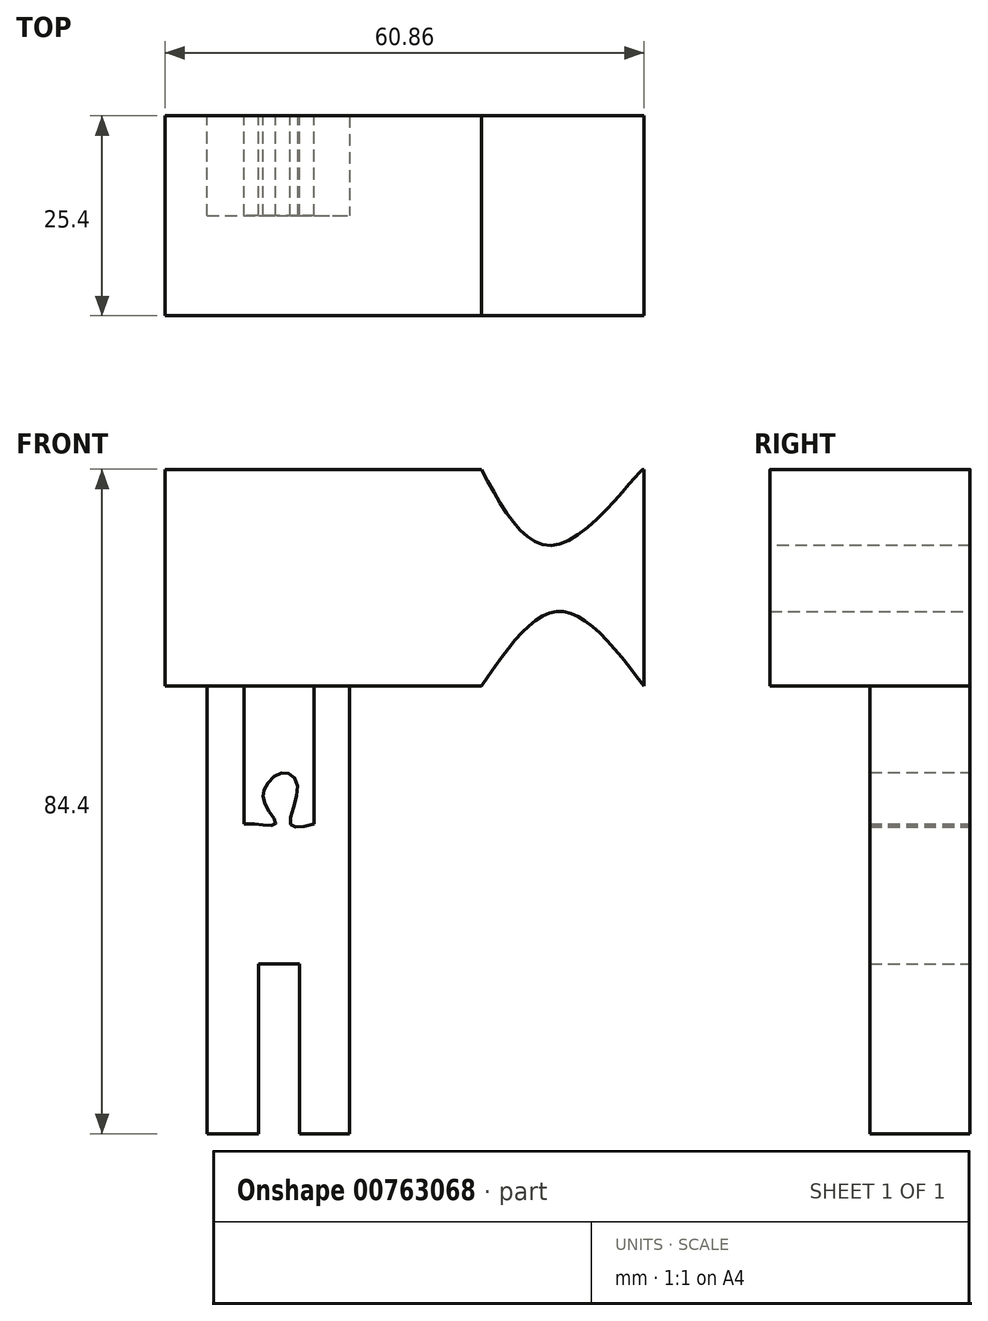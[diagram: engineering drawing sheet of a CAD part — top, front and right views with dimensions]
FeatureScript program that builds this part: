
annotation { "Feature Type Name" : "Feature", "Feature Type Description" : "" }
export const myFeature = defineFeature(function(context is Context, id is Id, definition is map)
    precondition{}
    {
        {
            var Q0;
            Q0=qCreatedBy(makeId("Front.planeOp"),FACE);
            var sketch = newSketch(context, id + "F0", { "sketchPlane" : qUnion([Q0])});
            skLineSegment(sketch, "E0", {"start": v(-46.17, 45.03) * mm, "end": v(-46.17, 17.54) * mm});
            skLineSegment(sketch, "E1", {"start": v(-46.17, 17.54) * mm, "end": v(-5.97, 17.54) * mm});
            skLineSegment(sketch, "E2", {"start": v(-46.17, 45.03) * mm, "end": v(-5.97, 45.03) * mm});
            skFitSpline(sketch, "E3", {"points": [v(-5.97, 45.03) * mm, v(3.89, 35.55) * mm, v(14.5, 45.03) * mm, v(14.7, 45.03) * mm], "startDerivative": vector(18.4, -33.95) * mm, "endDerivative": vector(2.33, -1.75) * mm});
            skFitSpline(sketch, "E4", {"points": [v(-5.97, 17.54) * mm, v(3.89, 27.02) * mm, v(14.7, 17.54) * mm], "startDerivative": vector(19.63, 28.56) * mm, "endDerivative": vector(21.7, -28.33) * mm});
            skLineSegment(sketch, "E5", {"start": v(14.65, 45.06) * mm, "end": v(14.7, 17.54) * mm});
            skSolve(sketch);
        }
        {
            var Q0;
            Q0=makeQuery(id+"F0.imprint","IMPRINT",FACE,{"disambiguationData":[TD([[makeQuery(id+"F0.imprint","IMPRINT",EDGE,{"derivedFrom":sQuery(id+"F0.wireOp",EDGE,"E0")}),1.0]])]});
            extrude(context, id + "F1", {"entities" : qUnion([Q0]), "depth" : 25.4 * mm, "offsetDistance" : 25.4 * mm});
        }
        {
            var Q0;
            Q0=qCreatedBy(makeId("Front.planeOp"),FACE);
            var sketch = newSketch(context, id + "F2", { "sketchPlane" : qUnion([Q0])});
            skLineSegment(sketch, "E6", {"start": v(-40.81, -39.33) * mm, "end": v(-34.26, -39.33) * mm});
            skLineSegment(sketch, "E7", {"start": v(-34.26, -39.33) * mm, "end": v(-34.26, -17.74) * mm});
            skLineSegment(sketch, "E8", {"start": v(-34.26, -17.74) * mm, "end": v(-29.05, -17.74) * mm});
            skLineSegment(sketch, "E9", {"start": v(-29.05, -17.74) * mm, "end": v(-29.05, -39.33) * mm});
            skLineSegment(sketch, "E10", {"start": v(-29.05, -39.33) * mm, "end": v(-22.7, -39.33) * mm});
            skLineSegment(sketch, "E11", {"start": v(-22.7, -39.33) * mm, "end": v(-22.7, -17.17) * mm});
            skLineSegment(sketch, "E12", {"start": v(-40.81, -17.17) * mm, "end": v(-40.81, -39.33) * mm});
            skLineSegment(sketch, "E13", {"start": v(-22.7, -17.17) * mm, "end": v(-22.7, 0) * mm});
            skLineSegment(sketch, "E14", {"start": v(-40.81, -17.17) * mm, "end": v(-40.81, 0) * mm});
            skLineSegment(sketch, "E15", {"start": v(-40.81, 0) * mm, "end": v(-40.81, 17.92) * mm});
            skLineSegment(sketch, "E16", {"start": v(-40.81, 17.92) * mm, "end": v(-36.12, 17.92) * mm});
            skLineSegment(sketch, "E17", {"start": v(-36.12, 17.92) * mm, "end": v(-36.12, 0) * mm});
            skLineSegment(sketch, "E18", {"start": v(-22.7, 0) * mm, "end": v(-22.7, 17.92) * mm});
            skLineSegment(sketch, "E19", {"start": v(-22.7, 17.92) * mm, "end": v(-27.2, 17.92) * mm});
            skLineSegment(sketch, "E20", {"start": v(-27.2, 17.92) * mm, "end": v(-27.2, 0) * mm});
            skFitSpline(sketch, "E21", {"points": [v(-27.2, 0) * mm, v(-30.24, 0) * mm, v(-29.3, 4.65) * mm, v(-31, 6.54) * mm, v(-33.46, 4.65) * mm, v(-33.27, 2.18) * mm, v(-32.14, 0) * mm, v(-34.8, 0) * mm, v(-36.12, 0) * mm], "startDerivative": vector(-31.27, -7.23) * mm, "endDerivative": vector(-11.83, -1.09) * mm});
            skSolve(sketch);
        }
        {
            var Q0;
            Q0=makeQuery(id+"F2.imprint","IMPRINT",FACE,{"disambiguationData":[TD([[makeQuery(id+"F2.imprint","IMPRINT",EDGE,{"derivedFrom":sQuery(id+"F2.wireOp",EDGE,"E6")}),1.0]])]});
            extrude(context, id + "F3", {"entities" : qUnion([Q0]), "operationType" : NewBodyOperationType.ADD, "depth" : 12.7 * mm, "offsetDistance" : 25.4 * mm});
        }
    });
